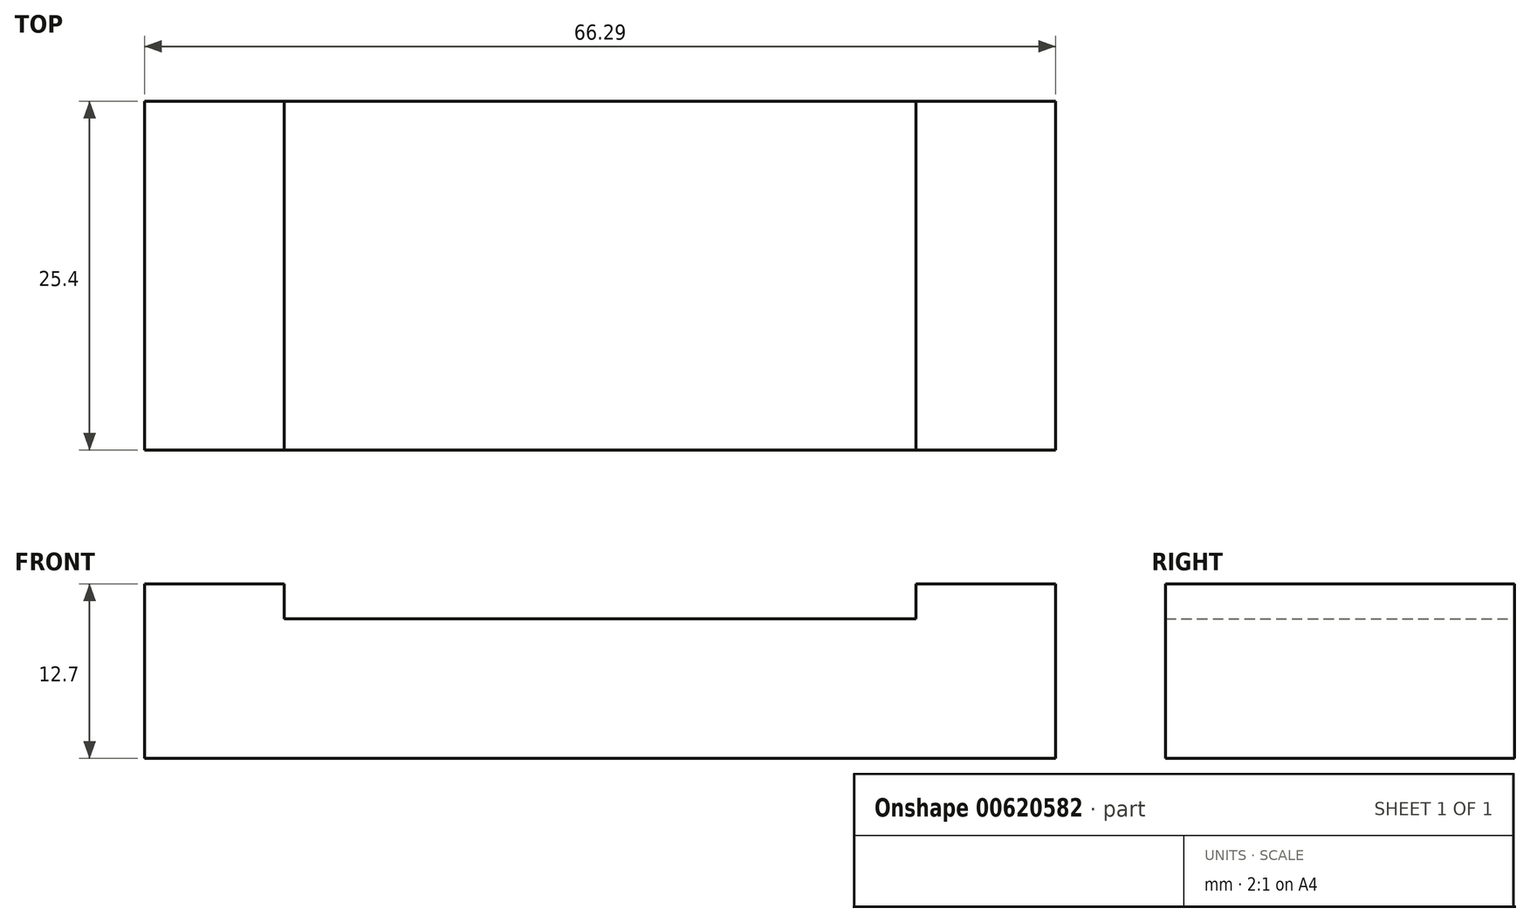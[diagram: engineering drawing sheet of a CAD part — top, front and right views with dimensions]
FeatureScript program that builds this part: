
annotation { "Feature Type Name" : "Feature", "Feature Type Description" : "" }
export const myFeature = defineFeature(function(context is Context, id is Id, definition is map)
    precondition{}
    {
        {
            var Q0;
            Q0=qCreatedBy(makeId("Front.planeOp"),FACE);
            var sketch = newSketch(context, id + "F0", { "sketchPlane" : qUnion([Q0])});
            skLineSegment(sketch, "E0", {"start": v(0, 0) * mm, "end": v(0, 12.7) * mm});
            skLineSegment(sketch, "E1", {"start": v(0, 12.7) * mm, "end": v(10.16, 12.7) * mm});
            skLineSegment(sketch, "E2", {"start": v(10.16, 12.7) * mm, "end": v(10.16, 10.16) * mm});
            skLineSegment(sketch, "E3", {"start": v(10.16, 10.16) * mm, "end": v(56.13, 10.16) * mm});
            skLineSegment(sketch, "E4", {"start": v(56.13, 10.16) * mm, "end": v(56.13, 12.7) * mm});
            skLineSegment(sketch, "E5", {"start": v(56.13, 12.7) * mm, "end": v(66.3, 12.7) * mm});
            skLineSegment(sketch, "E6", {"start": v(66.3, 12.7) * mm, "end": v(66.3, 0) * mm});
            skLineSegment(sketch, "E7", {"start": v(66.3, 0) * mm, "end": v(0, 0) * mm});
            skLineSegment(sketch, "E8", {"start": v(5.84, 15.24) * mm, "end": v(-0.5, 15.24) * mm});
            skLineSegment(sketch, "E9", {"start": v(-0.5, 15.24) * mm, "end": v(-10.88, 3.85) * mm});
            skLineSegment(sketch, "E10", {"start": v(0, 0) * mm, "end": v(-6.65, 0) * mm});
            skCircle(sketch, "E11", {"center": v(-6.65, 0) * mm, "radius": 5.72 * mm});
            skCircle(sketch, "E12", {"center": v(-6.65, 0) * mm, "radius": 3.18 * mm});
            skLineSegment(sketch, "E13", {"start": v(5.84, 15.24) * mm, "end": v(5.84, -9.4) * mm});
            skLineSegment(sketch, "E14", {"start": v(5.84, -9.4) * mm, "end": v(-8.18, -5.5) * mm});
            skSolve(sketch);
        }
        {
            var Q0;
            {var subQ0=sQuery(id+"F0.wireOp",EDGE,"E2");Q0=makeQuery(id+"F0.imprint","IMPRINT",FACE,{"disambiguationData":[TD([[makeQuery(id+"F0.imprint","IMPRINT",EDGE,{"derivedFrom":subQ0}),-1.0]])]});}
            extrude(context, id + "F1", {"entities" : qUnion([Q0]), "endBound" : BoundingType.SYMMETRIC, "depth" : 25.4 * mm, "offsetDistance" : 25.4 * mm});
        }
        {
            var Q0;
            {var subQ0=sQuery(id+"F0.wireOp",EDGE,"E0");Q0=makeQuery(id+"F0.imprint","IMPRINT",FACE,{"disambiguationData":[TD([[makeQuery(id+"F0.imprint","IMPRINT",EDGE,{"derivedFrom":subQ0}),-1.0]])]});}
            extrude(context, id + "F2", {"entities" : qUnion([Q0]), "operationType" : NewBodyOperationType.ADD, "endBound" : BoundingType.SYMMETRIC, "depth" : 25.4 * mm, "offsetDistance" : 25.4 * mm});
        }
    });
